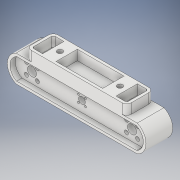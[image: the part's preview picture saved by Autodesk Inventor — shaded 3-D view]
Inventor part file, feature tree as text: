
AUTODESK INVENTOR PART (.ipt)
format: ipt  version: 2019 (Build 230136000, 136)  size: 337,408 bytes
history: native  units: mm
features: extrude x11, sketch x11, projected_geometry x11
ambient origin geometry x8: Origin, YZ Plane, XZ Plane, XY Plane, X Axis, Y Axis, Z Axis, Center Point
bodies: Solid1 (feature_tree)
feature tree (33):
  extrude  "Extrusion1"  Depth=75.0mm
  extrude  "Extrusion2"  Depth=75.0mm
  extrude  "Extrusion3"  Depth=90.0mm
  extrude  "Extrusion4"  Depth=90.0mm
  extrude  "Extrusion5"  Depth=30.0mm TaperAngle=0.0deg
  extrude  "Extrusion6"  Depth=30.0mm TaperAngle=0.0deg
  extrude  "Extrusion7"  Depth=33.0mm
  extrude  "Extrusion8"  Depth=5.0mm TaperAngle=0.0deg
  extrude  "Extrusion11"  Depth=5.0mm TaperAngle=0.0deg
  extrude  "Extrusion12"  Depth=1.0mm TaperAngle=0.0deg
  extrude  "Extrusion13"  Depth=7.0mm TaperAngle=0.0deg
  sketch  "Sketch1"  dims[d4=10.0mm d5=75.0mm]
  sketch  "Sketch2"  dims[d6=75.0mm d7=200.0mm]
  projected_geometry  "Projected Loop1"
  sketch  "Sketch3"  dims[d8=32.0mm d9=90.0mm]
  projected_geometry  "Projected Loop2"
  sketch  "Sketch4"  dims[d10=90.0mm d11=90.0mm]
  projected_geometry  "Projected Loop3"
  sketch  "Sketch5"  dims[d12=90.0mm d13=30.0mm d14=0.0mm]
  projected_geometry  "Projected Loop4"
  sketch  "Sketch6"  dims[d15=4.0mm d16=30.0mm d17=0.0mm]
  projected_geometry  "Projected Loop5"
  projected_geometry  "Projected Loop6"
  sketch  "Sketch7"  dims[d18=24.0mm d19=33.0mm]
  projected_geometry  "Projected Loop7"
  sketch  "Sketch8"  dims[d20=33.0mm d21=5.0mm d22=0.0mm]
  projected_geometry  "Projected Loop8"
  sketch  "Sketch10"  dims[d23=4.0mm d24=5.0mm d25=0.0mm]
  projected_geometry  "Projected Loop10"
  sketch  "Sketch11"  dims[d26=2.0mm d27=0.0mm d28=1.0mm d29=0.0mm]
  projected_geometry  "Projected Loop11"
  sketch  "Sketch12"  dims[d30=10.0mm d31=0.0mm d32=7.0mm d33=0.0mm d47=4.0mm d48=20.0mm d49=20.0mm d50=15.0mm d51=0.0mm d52=85.0mm d53=0.0mm d54=120.0mm d55=18.0mm d56=5.0mm d57=5.0mm d58=0.0mm]
  projected_geometry  "Projected Loop12"
